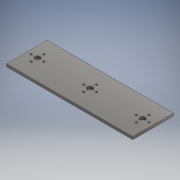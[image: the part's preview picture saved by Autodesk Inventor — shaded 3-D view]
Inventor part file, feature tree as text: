
AUTODESK INVENTOR PART (.ipt)
format: ipt  version: 2018 (Build 220112000, 112)  size: 133,120 bytes
history: native  units: mm
features: other x1, extrude x1, sketch x1
ambient origin geometry x8: Origin, YZ Plane, XZ Plane, XY Plane, X Axis, Y Axis, Z Axis, Center Point
bodies: Body1 (feature_tree)
feature tree (3):
  other  "Sólido1"
  extrude  "Extrusión1"  Depth=29.0mm
  sketch  "Boceto1"  dims[d0=90.0mm d1=29.0mm d2=4.0mm d8=1.5mm d9=1.5mm d10=1.5mm d11=1.5mm d23=4.0mm d25=1.5mm d28=1.5mm d29=1.5mm d35=4.0mm d36=1.5mm d37=1.5mm d38=1.5mm d39=1.5mm d40=2.0mm d41=0.0mm]
